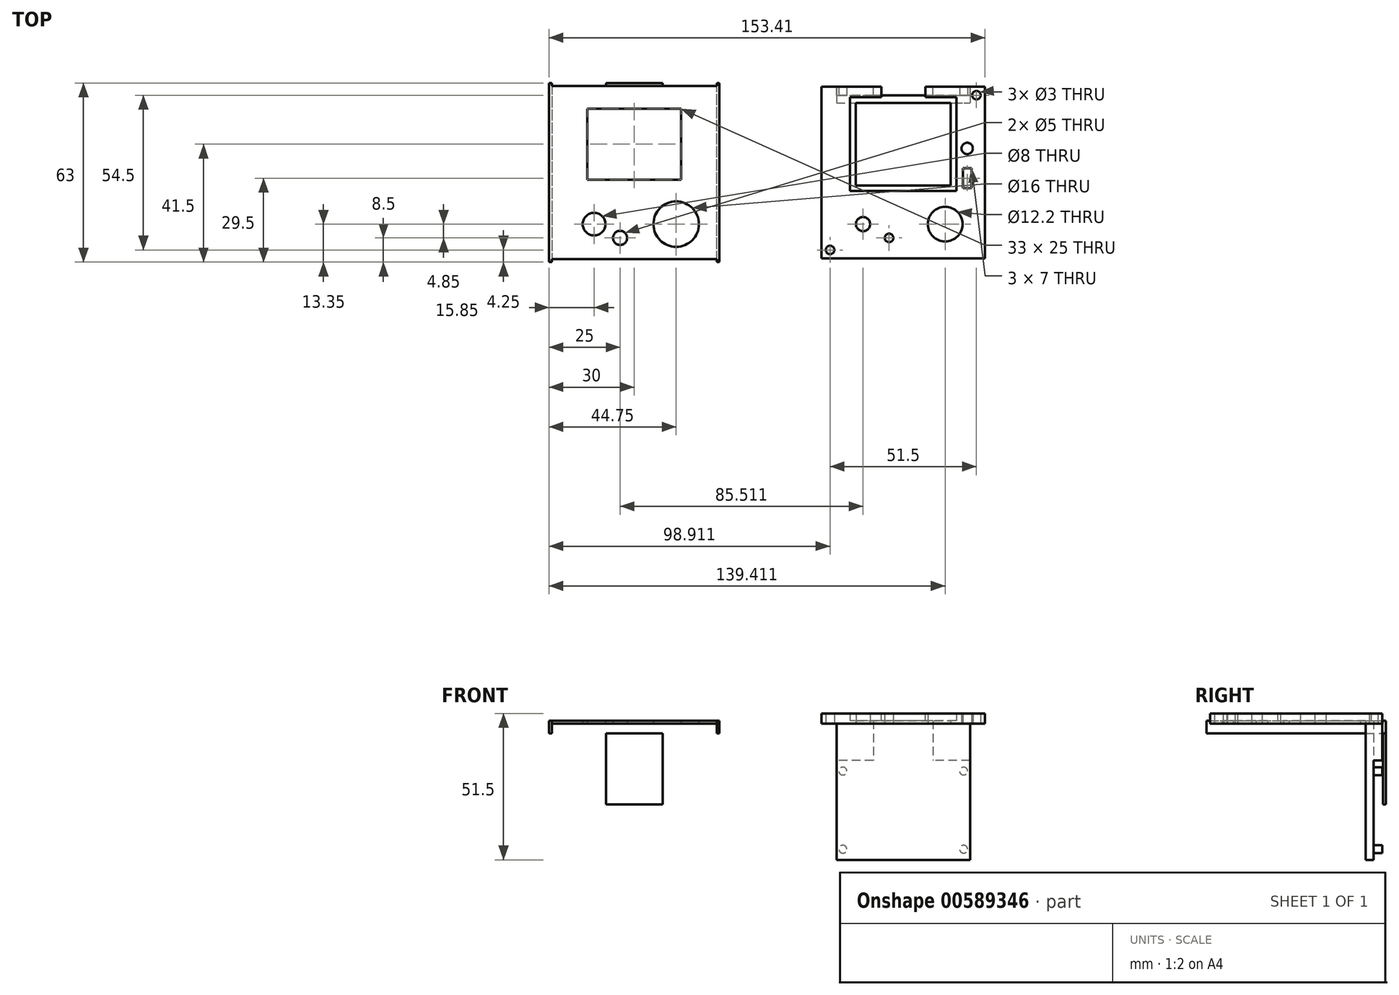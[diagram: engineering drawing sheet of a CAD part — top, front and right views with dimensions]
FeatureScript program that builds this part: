
annotation { "Feature Type Name" : "Feature", "Feature Type Description" : "" }
export const myFeature = defineFeature(function(context is Context, id is Id, definition is map)
    precondition{}
    {
        {
            var Q0;
            Q0=qCreatedBy(makeId("Top.planeOp"),FACE);
            var sketch = newSketch(context, id + "F0", { "sketchPlane" : qUnion([Q0])});
            skLineSegment(sketch, "E0.bottom", {"start": v(29, -30.5) * mm, "end": v(-29, -30.5) * mm});
            skLineSegment(sketch, "E0.top", {"start": v(29, 30.5) * mm, "end": v(-29, 30.5) * mm});
            skLineSegment(sketch, "E0.left", {"start": v(29, -30.5) * mm, "end": v(29, 30.5) * mm});
            skLineSegment(sketch, "E0.right", {"start": v(-29, -30.5) * mm, "end": v(-29, 30.5) * mm});
            skPoint(sketch, "E0.middle", {"position": v(0, 0) * mm});
            skPoint(sketch, "E1.middle", {"position": v(0, 10) * mm});
            skLineSegment(sketch, "E2.bottom", {"start": v(15.75, 22) * mm, "end": v(-15.75, 22) * mm, "construction": true});
            skLineSegment(sketch, "E2.top", {"start": v(15.75, -2) * mm, "end": v(-15.75, -2) * mm, "construction": true});
            skLineSegment(sketch, "E2.left", {"start": v(15.75, 22) * mm, "end": v(15.75, -2) * mm, "construction": true});
            skLineSegment(sketch, "E2.right", {"start": v(-15.75, 22) * mm, "end": v(-15.75, -2) * mm, "construction": true});
            skLineSegment(sketch, "E3.bottom", {"start": v(16.5, -2.5) * mm, "end": v(-16.5, -2.5) * mm});
            skLineSegment(sketch, "E3.top", {"start": v(16.5, 22.5) * mm, "end": v(-16.5, 22.5) * mm});
            skLineSegment(sketch, "E3.left", {"start": v(16.5, -2.5) * mm, "end": v(16.5, 22.5) * mm});
            skLineSegment(sketch, "E3.right", {"start": v(-16.5, -2.5) * mm, "end": v(-16.5, 22.5) * mm});
            skLineSegment(sketch, "E4.bottom", {"start": v(18.5, -6.5) * mm, "end": v(-18.5, -6.5) * mm, "construction": true});
            skLineSegment(sketch, "E4.top", {"start": v(18.5, 26.5) * mm, "end": v(-18.5, 26.5) * mm, "construction": true});
            skLineSegment(sketch, "E4.left", {"start": v(18.5, -6.5) * mm, "end": v(18.5, 26.5) * mm, "construction": true});
            skLineSegment(sketch, "E4.right", {"start": v(-18.5, -6.5) * mm, "end": v(-18.5, 26.5) * mm, "construction": true});
            skLineSegment(sketch, "E5.bottom", {"start": v(-29, 30.5) * mm, "end": v(29, 30.5) * mm});
            skLineSegment(sketch, "E5.top", {"start": v(-29, 31.5) * mm, "end": v(29, 31.5) * mm});
            skLineSegment(sketch, "E5.left", {"start": v(-29, 30.5) * mm, "end": v(-29, 31.5) * mm});
            skLineSegment(sketch, "E5.right", {"start": v(29, 30.5) * mm, "end": v(29, 31.5) * mm});
            skLineSegment(sketch, "E6.bottom", {"start": v(-29, -30.5) * mm, "end": v(29, -30.5) * mm});
            skLineSegment(sketch, "E6.top", {"start": v(-29, -31.5) * mm, "end": v(29, -31.5) * mm});
            skLineSegment(sketch, "E6.left", {"start": v(-29, -30.5) * mm, "end": v(-29, -31.5) * mm});
            skLineSegment(sketch, "E6.right", {"start": v(29, -30.5) * mm, "end": v(29, -31.5) * mm});
            skLineSegment(sketch, "E7.bottom", {"start": v(-29, -31.5) * mm, "end": v(-30, -31.5) * mm});
            skLineSegment(sketch, "E7.top", {"start": v(-29, 31.5) * mm, "end": v(-30, 31.5) * mm});
            skLineSegment(sketch, "E7.left", {"start": v(-29, -31.5) * mm, "end": v(-29, 31.5) * mm});
            skLineSegment(sketch, "E7.right", {"start": v(-30, -31.5) * mm, "end": v(-30, 31.5) * mm});
            skLineSegment(sketch, "E8.bottom", {"start": v(29, -31.5) * mm, "end": v(30, -31.5) * mm});
            skLineSegment(sketch, "E8.top", {"start": v(29, 31.5) * mm, "end": v(30, 31.5) * mm});
            skLineSegment(sketch, "E8.left", {"start": v(29, -31.5) * mm, "end": v(29, 31.5) * mm});
            skLineSegment(sketch, "E8.right", {"start": v(30, -31.5) * mm, "end": v(30, 31.5) * mm});
            skCircle(sketch, "E9", {"center": v(14.75, -18.15) * mm, "radius": 8 * mm});
            skCircle(sketch, "E10", {"center": v(-14.15, -18.15) * mm, "radius": 4 * mm});
            skCircle(sketch, "E11", {"center": v(-5, -23) * mm, "radius": 2.5 * mm});
            skSolve(sketch);
        }
        {
            var Q0;
            Q0=qCreatedBy(makeId("Top.planeOp"),FACE);
            var sketch = newSketch(context, id + "F1", { "sketchPlane" : qUnion([Q0])});
            skLineSegment(sketch, "E12.bottom", {"start": v(123.41, -30.25) * mm, "end": v(65.91, -30.25) * mm});
            skLineSegment(sketch, "E12.top", {"start": v(123.41, 30.25) * mm, "end": v(65.91, 30.25) * mm});
            skLineSegment(sketch, "E12.left", {"start": v(123.41, -30.25) * mm, "end": v(123.41, 30.25) * mm});
            skLineSegment(sketch, "E12.right", {"start": v(65.91, -30.25) * mm, "end": v(65.91, 30.25) * mm});
            skPoint(sketch, "E12.middle", {"position": v(94.66, 0) * mm});
            skLineSegment(sketch, "E13.bottom", {"start": v(113.41, -6.5) * mm, "end": v(75.91, -6.5) * mm});
            skLineSegment(sketch, "E13.top", {"start": v(113.41, 26.5) * mm, "end": v(75.91, 26.5) * mm});
            skLineSegment(sketch, "E13.left", {"start": v(113.41, -6.5) * mm, "end": v(113.41, 26.5) * mm});
            skLineSegment(sketch, "E13.right", {"start": v(75.91, -6.5) * mm, "end": v(75.91, 26.5) * mm});
            skPoint(sketch, "E13.middle", {"position": v(94.66, 10) * mm});
            skCircle(sketch, "E14", {"center": v(68.91, -27.25) * mm, "radius": 1.5 * mm});
            skCircle(sketch, "E15", {"center": v(120.41, 27.25) * mm, "radius": 1.5 * mm});
            skCircle(sketch, "E16", {"center": v(109.41, -18.15) * mm, "radius": 6.1 * mm});
            skLineSegment(sketch, "E17.bottom", {"start": v(115.66, 1.5) * mm, "end": v(118.66, 1.5) * mm});
            skLineSegment(sketch, "E17.top", {"start": v(115.66, -5.5) * mm, "end": v(118.66, -5.5) * mm});
            skLineSegment(sketch, "E17.left", {"start": v(115.66, 1.5) * mm, "end": v(115.66, -5.5) * mm});
            skLineSegment(sketch, "E17.right", {"start": v(118.66, 1.5) * mm, "end": v(118.66, -5.5) * mm});
            skCircle(sketch, "E18", {"center": v(117.16, 8.5) * mm, "radius": 2 * mm});
            skPoint(sketch, "E18.centerSnap0", {"position": v(117.16, 1.5) * mm});
            skCircle(sketch, "E19", {"center": v(80.51, -18.15) * mm, "radius": 2.5 * mm});
            skCircle(sketch, "E20", {"center": v(89.66, -23) * mm, "radius": 1.5 * mm});
            skSolve(sketch);
        }
        {
            var Q0;
            Q0=makeQuery(id+"F1.imprint","IMPRINT",FACE,{"disambiguationData":[TD([[makeQuery(id+"F1.imprint","IMPRINT",EDGE,{"derivedFrom":sQuery(id+"F1.wireOp",EDGE,"E12.bottom")}),-1.0]])]});
            extrude(context, id + "F2", {"entities" : qUnion([Q0]), "depth" : 3.5 * mm});
        }
        {
            var Q0;
            Q0=makeQuery(id+"F2.opExtrude","CAP_FACE",FACE,{"disambiguationData":[OSD([sQuery(id+"F1.wireOp",EDGE,"E12.bottom"),sQuery(id+"F1.wireOp",EDGE,"E12.top"),sQuery(id+"F1.wireOp",EDGE,"E12.left"),sQuery(id+"F1.wireOp",EDGE,"E12.right"),sQuery(id+"F1.wireOp",EDGE,"E13.bottom"),sQuery(id+"F1.wireOp",EDGE,"E13.top"),sQuery(id+"F1.wireOp",EDGE,"E13.left"),sQuery(id+"F1.wireOp",EDGE,"E13.right"),sQuery(id+"F1.wireOp",EDGE,"E14"),sQuery(id+"F1.wireOp",EDGE,"E15"),sQuery(id+"F1.wireOp",EDGE,"E16"),sQuery(id+"F1.wireOp",EDGE,"E17.bottom"),sQuery(id+"F1.wireOp",EDGE,"E17.top"),sQuery(id+"F1.wireOp",EDGE,"E17.left"),sQuery(id+"F1.wireOp",EDGE,"E17.right"),sQuery(id+"F1.wireOp",EDGE,"E18"),sQuery(id+"F1.wireOp",EDGE,"E19"),sQuery(id+"F1.wireOp",EDGE,"E20")])],"isStart":false});
            var sketch = newSketch(context, id + "F3", { "sketchPlane" : qUnion([Q0])});
            skLineSegment(sketch, "E21.bottom", {"start": v(102.41, 26.5) * mm, "end": v(86.91, 26.5) * mm});
            skLineSegment(sketch, "E21.top", {"start": v(102.41, 30.25) * mm, "end": v(86.91, 30.25) * mm});
            skLineSegment(sketch, "E21.left", {"start": v(102.41, 26.5) * mm, "end": v(102.41, 30.25) * mm});
            skLineSegment(sketch, "E21.right", {"start": v(86.91, 26.5) * mm, "end": v(86.91, 30.25) * mm});
            skPoint(sketch, "E21.middle", {"position": v(94.66, 28.38) * mm});
            skPoint(sketch, "E21.middle.positionSnap0", {"position": v(94.66, 26.5) * mm});
            skPoint(sketch, "E21.centerSnap0", {"position": v(94.66, 26.5) * mm});
            skSolve(sketch);
        }
        {
            var Q0;
            Q0=makeQuery(id+"F2.opExtrude","CAP_FACE",FACE,{"disambiguationData":[OSD([sQuery(id+"F1.wireOp",EDGE,"E12.bottom"),sQuery(id+"F1.wireOp",EDGE,"E12.top"),sQuery(id+"F1.wireOp",EDGE,"E12.left"),sQuery(id+"F1.wireOp",EDGE,"E12.right"),sQuery(id+"F1.wireOp",EDGE,"E13.bottom"),sQuery(id+"F1.wireOp",EDGE,"E13.top"),sQuery(id+"F1.wireOp",EDGE,"E13.left"),sQuery(id+"F1.wireOp",EDGE,"E13.right"),sQuery(id+"F1.wireOp",EDGE,"E14"),sQuery(id+"F1.wireOp",EDGE,"E15"),sQuery(id+"F1.wireOp",EDGE,"E16"),sQuery(id+"F1.wireOp",EDGE,"E17.bottom"),sQuery(id+"F1.wireOp",EDGE,"E17.top"),sQuery(id+"F1.wireOp",EDGE,"E17.left"),sQuery(id+"F1.wireOp",EDGE,"E17.right"),sQuery(id+"F1.wireOp",EDGE,"E18"),sQuery(id+"F1.wireOp",EDGE,"E19"),sQuery(id+"F1.wireOp",EDGE,"E20")])],"isStart":true});
            var sketch = newSketch(context, id + "F4", { "sketchPlane" : qUnion([Q0])});
            skLineSegment(sketch, "E22.bottom", {"start": v(75.91, -26.5) * mm, "end": v(113.41, -26.5) * mm});
            skLineSegment(sketch, "E22.top", {"start": v(75.91, 6.5) * mm, "end": v(113.41, 6.5) * mm});
            skLineSegment(sketch, "E22.left", {"start": v(75.91, -26.5) * mm, "end": v(75.91, 6.5) * mm});
            skLineSegment(sketch, "E22.right", {"start": v(113.41, -26.5) * mm, "end": v(113.41, 6.5) * mm});
            skLineSegment(sketch, "E23.0", {"start": v(111.41, -24.5) * mm, "end": v(111.41, 4.5) * mm});
            skLineSegment(sketch, "E23.1", {"start": v(77.91, -24.5) * mm, "end": v(111.41, -24.5) * mm});
            skLineSegment(sketch, "E23.2", {"start": v(77.91, -24.5) * mm, "end": v(77.91, 4.5) * mm});
            skLineSegment(sketch, "E23.3", {"start": v(77.91, 4.5) * mm, "end": v(111.41, 4.5) * mm});
            skSolve(sketch);
        }
        {
            var Q0;
            Q0=makeQuery(id+"F4.imprint","IMPRINT",FACE,{"disambiguationData":[TD([[makeQuery(id+"F4.imprint","IMPRINT",EDGE,{"derivedFrom":sQuery(id+"F4.wireOp",EDGE,"E22.bottom")}),-1.0]])]});
            extrude(context, id + "F5", {"entities" : qUnion([Q0]), "operationType" : NewBodyOperationType.ADD, "oppositeDirection" : true, "depth" : 1 * mm});
        }
        {
            var Q0;
            Q0=makeQuery(id+"F3.imprint","IMPRINT",FACE,{"disambiguationData":[TD([[makeQuery(id+"F3.imprint","IMPRINT",EDGE,{"derivedFrom":sQuery(id+"F3.wireOp",EDGE,"E21.bottom")}),-1.0]])]});
            extrude(context, id + "F6", {"entities" : qUnion([Q0]), "operationType" : NewBodyOperationType.REMOVE, "oppositeDirection" : true, "depth" : 2.5 * mm});
        }
        {
            var Q0;
            Q0=makeQuery(id+"F5.opExtrude","SWEPT_FACE",FACE,{"disambiguationData":[OSD([sQuery(id+"F4.wireOp",EDGE,"E23.1")])]});
            var sketch = newSketch(context, id + "F7", { "sketchPlane" : qUnion([Q0])});
            skLineSegment(sketch, "E24.bottom", {"start": v(71.16, 0) * mm, "end": v(118.16, 0) * mm});
            skLineSegment(sketch, "E24.top", {"start": v(71.16, -48) * mm, "end": v(118.16, -48) * mm});
            skLineSegment(sketch, "E24.left", {"start": v(71.16, 0) * mm, "end": v(71.16, -48) * mm});
            skLineSegment(sketch, "E24.right", {"start": v(118.16, 0) * mm, "end": v(118.16, -48) * mm});
            skSolve(sketch);
        }
        {
            var Q0;
            Q0=makeQuery(id+"F7.imprint","IMPRINT",FACE,{"disambiguationData":[TD([[makeQuery(id+"F7.imprint","IMPRINT",EDGE,{"derivedFrom":sQuery(id+"F7.wireOp",EDGE,"E24.bottom")}),-1.0]])]});
            extrude(context, id + "F8", {"entities" : qUnion([Q0]), "operationType" : NewBodyOperationType.ADD, "oppositeDirection" : true, "depth" : 5.75 * mm});
        }
        {
            var Q0;
            Q0=makeQuery(id+"F8.boolean.opBoolean","MERGE",FACE,{"derivedFrom":[makeQuery(id+"F2.opExtrude","SWEPT_FACE",FACE,{"disambiguationData":[OSD([sQuery(id+"F1.wireOp",EDGE,"E12.top")])]}),makeQuery(id+"F8.opExtrude","CAP_FACE",FACE,{"disambiguationData":[OSD([sQuery(id+"F7.wireOp",EDGE,"E24.bottom"),sQuery(id+"F7.wireOp",EDGE,"E24.top"),sQuery(id+"F7.wireOp",EDGE,"E24.left"),sQuery(id+"F7.wireOp",EDGE,"E24.right")])],"isStart":false})]});
            var sketch = newSketch(context, id + "F9", { "sketchPlane" : qUnion([Q0])});
            skLineSegment(sketch, "E25.bottom", {"start": v(-118.16, -13) * mm, "end": v(-71.16, -13) * mm});
            skLineSegment(sketch, "E25.top", {"start": v(-118.16, -48) * mm, "end": v(-71.16, -48) * mm});
            skLineSegment(sketch, "E25.left", {"start": v(-118.16, -13) * mm, "end": v(-118.16, -48) * mm});
            skLineSegment(sketch, "E25.right", {"start": v(-71.16, -13) * mm, "end": v(-71.16, -48) * mm});
            skLineSegment(sketch, "E26.bottom", {"start": v(-105.16, 1) * mm, "end": v(-84.16, 1) * mm});
            skLineSegment(sketch, "E26.top", {"start": v(-105.16, -13) * mm, "end": v(-86.91, -13) * mm});
            skLineSegment(sketch, "E26.left", {"start": v(-105.16, 1) * mm, "end": v(-105.16, -13) * mm});
            skLineSegment(sketch, "E26.right", {"start": v(-84.16, 1) * mm, "end": v(-84.16, -13) * mm});
            skSolve(sketch);
        }
        {
            var Q0;
            Q0=makeQuery(id+"F9.imprint","IMPRINT",FACE,{"disambiguationData":[TD([[makeQuery(id+"F9.imprint","IMPRINT",EDGE,{"derivedFrom":sQuery(id+"F9.wireOp",EDGE,"E25.top")}),-1.0]])]});
            var Q1;
            Q1=makeQuery(id+"F9.imprint","IMPRINT",FACE,{"disambiguationData":[TD([[makeQuery(id+"F9.imprint","IMPRINT",EDGE,{"derivedFrom":sQuery(id+"F9.wireOp",EDGE,"E26.bottom")}),-1.0]])]});
            extrude(context, id + "F10", {"entities" : qUnion([Q0, Q1]), "operationType" : NewBodyOperationType.REMOVE, "oppositeDirection" : true, "depth" : 3 * mm});
        }
        {
            var Q0;
            Q0=makeQuery(id+"F10.boolean.opBoolean","COPY",FACE,{"derivedFrom":makeQuery(id+"F10.opExtrude","CAP_FACE",FACE,{"disambiguationData":[OSD([sQuery(id+"F9.wireOp",EDGE,"E25.bottom"),sQuery(id+"F9.wireOp",EDGE,"E25.top"),sQuery(id+"F9.wireOp",EDGE,"E25.left"),sQuery(id+"F9.wireOp",EDGE,"E25.right"),sQuery(id+"F9.wireOp",EDGE,"E26.bottom"),sQuery(id+"F9.wireOp",EDGE,"E26.left"),sQuery(id+"F9.wireOp",EDGE,"E26.right")])],"isStart":false})});
            var sketch = newSketch(context, id + "F11", { "sketchPlane" : qUnion([Q0])});
            skCircle(sketch, "E27", {"center": v(-115.91, -16.75) * mm, "radius": 1.4 * mm});
            skCircle(sketch, "E28", {"center": v(-115.91, -44.25) * mm, "radius": 1.4 * mm});
            skCircle(sketch, "E29", {"center": v(-73.41, -16.75) * mm, "radius": 1.4 * mm});
            skCircle(sketch, "E30", {"center": v(-73.41, -44.25) * mm, "radius": 1.4 * mm});
            skSolve(sketch);
        }
        {
            var Q0;
            Q0=qSketchRegion(id+"F11",true);
            extrude(context, id + "F12", {"entities" : qUnion([Q0]), "operationType" : NewBodyOperationType.ADD, "depth" : 3 * mm});
        }
        {
            var Q0;
            Q0=makeQuery(id+"F0.imprint","IMPRINT",FACE,{"disambiguationData":[TD([[makeQuery(id+"F0.imprint","IMPRINT",EDGE,{"derivedFrom":sQuery(id+"F0.wireOp",EDGE,"E3.bottom")}),1.0]])]});
            var Q1;
            {var subQ3=sQuery(id+"F0.wireOp",EDGE,"E7.bottom");Q1=makeQuery(id+"F0.imprint","IMPRINT",FACE,{"disambiguationData":[TD([[makeQuery(id+"F0.imprint","IMPRINT",EDGE,{"derivedFrom":subQ3}),-1.0]])]});}
            var Q2;
            {var subQ0=sQuery(id+"F0.wireOp",EDGE,"E5.bottom");Q2=makeQuery(id+"F0.imprint","IMPRINT",FACE,{"disambiguationData":[TD([[makeQuery(id+"F0.imprint","IMPRINT",EDGE,{"derivedFrom":subQ0}),1.0]])]});}
            var Q3;
            {var subQ3=sQuery(id+"F0.wireOp",EDGE,"E8.bottom");Q3=makeQuery(id+"F0.imprint","IMPRINT",FACE,{"disambiguationData":[TD([[makeQuery(id+"F0.imprint","IMPRINT",EDGE,{"derivedFrom":subQ3}),1.0]])]});}
            var Q4;
            {var subQ0=sQuery(id+"F0.wireOp",EDGE,"E6.bottom");Q4=makeQuery(id+"F0.imprint","IMPRINT",FACE,{"disambiguationData":[TD([[makeQuery(id+"F0.imprint","IMPRINT",EDGE,{"derivedFrom":subQ0}),-1.0]])]});}
            extrude(context, id + "F13", {"entities" : qUnion([Q0, Q1, Q2, Q3, Q4]), "depth" : 1 * mm});
        }
        {
            var Q0;
            {var subQ0=sQuery(id+"F0.wireOp",EDGE,"E5.bottom");Q0=makeQuery(id+"F0.imprint","IMPRINT",FACE,{"disambiguationData":[TD([[makeQuery(id+"F0.imprint","IMPRINT",EDGE,{"derivedFrom":subQ0}),1.0]])]});}
            var Q1;
            {var subQ3=sQuery(id+"F0.wireOp",EDGE,"E7.bottom");Q1=makeQuery(id+"F0.imprint","IMPRINT",FACE,{"disambiguationData":[TD([[makeQuery(id+"F0.imprint","IMPRINT",EDGE,{"derivedFrom":subQ3}),-1.0]])]});}
            var Q2;
            {var subQ0=sQuery(id+"F0.wireOp",EDGE,"E6.bottom");Q2=makeQuery(id+"F0.imprint","IMPRINT",FACE,{"disambiguationData":[TD([[makeQuery(id+"F0.imprint","IMPRINT",EDGE,{"derivedFrom":subQ0}),-1.0]])]});}
            var Q3;
            {var subQ3=sQuery(id+"F0.wireOp",EDGE,"E8.bottom");Q3=makeQuery(id+"F0.imprint","IMPRINT",FACE,{"disambiguationData":[TD([[makeQuery(id+"F0.imprint","IMPRINT",EDGE,{"derivedFrom":subQ3}),1.0]])]});}
            extrude(context, id + "F14", {"entities" : qUnion([Q0, Q1, Q2, Q3]), "operationType" : NewBodyOperationType.ADD, "oppositeDirection" : true, "depth" : 3.5 * mm});
        }
        {
            var Q0;
            Q0=makeQuery(id+"F14.opExtrude","CAP_FACE",FACE,{"disambiguationData":[OSD([sQuery(id+"F0.wireOp",EDGE,"E5.bottom"),sQuery(id+"F0.wireOp",EDGE,"E5.top"),sQuery(id+"F0.wireOp",EDGE,"E6.bottom"),sQuery(id+"F0.wireOp",EDGE,"E6.top"),sQuery(id+"F0.wireOp",EDGE,"E7.bottom"),sQuery(id+"F0.wireOp",EDGE,"E7.top"),sQuery(id+"F0.wireOp",EDGE,"E7.left"),sQuery(id+"F0.wireOp",EDGE,"E7.right"),sQuery(id+"F0.wireOp",EDGE,"E8.bottom"),sQuery(id+"F0.wireOp",EDGE,"E8.top"),sQuery(id+"F0.wireOp",EDGE,"E8.left"),sQuery(id+"F0.wireOp",EDGE,"E8.right")])],"isStart":false});
            var sketch = newSketch(context, id + "F15", { "sketchPlane" : qUnion([Q0])});
            skLineSegment(sketch, "E31.bottom", {"start": v(10, -31.5) * mm, "end": v(-10, -31.5) * mm});
            skLineSegment(sketch, "E31.top", {"start": v(10, -30.5) * mm, "end": v(-10, -30.5) * mm});
            skLineSegment(sketch, "E31.left", {"start": v(10, -31.5) * mm, "end": v(10, -30.5) * mm});
            skLineSegment(sketch, "E31.right", {"start": v(-10, -31.5) * mm, "end": v(-10, -30.5) * mm});
            skPoint(sketch, "E32", {"position": v(0, -30.5) * mm});
            skSolve(sketch);
        }
        {
            var Q0;
            Q0=qSketchRegion(id+"F15",true);
            extrude(context, id + "F16", {"entities" : qUnion([Q0]), "operationType" : NewBodyOperationType.ADD, "depth" : 25 * mm});
        }
    });
